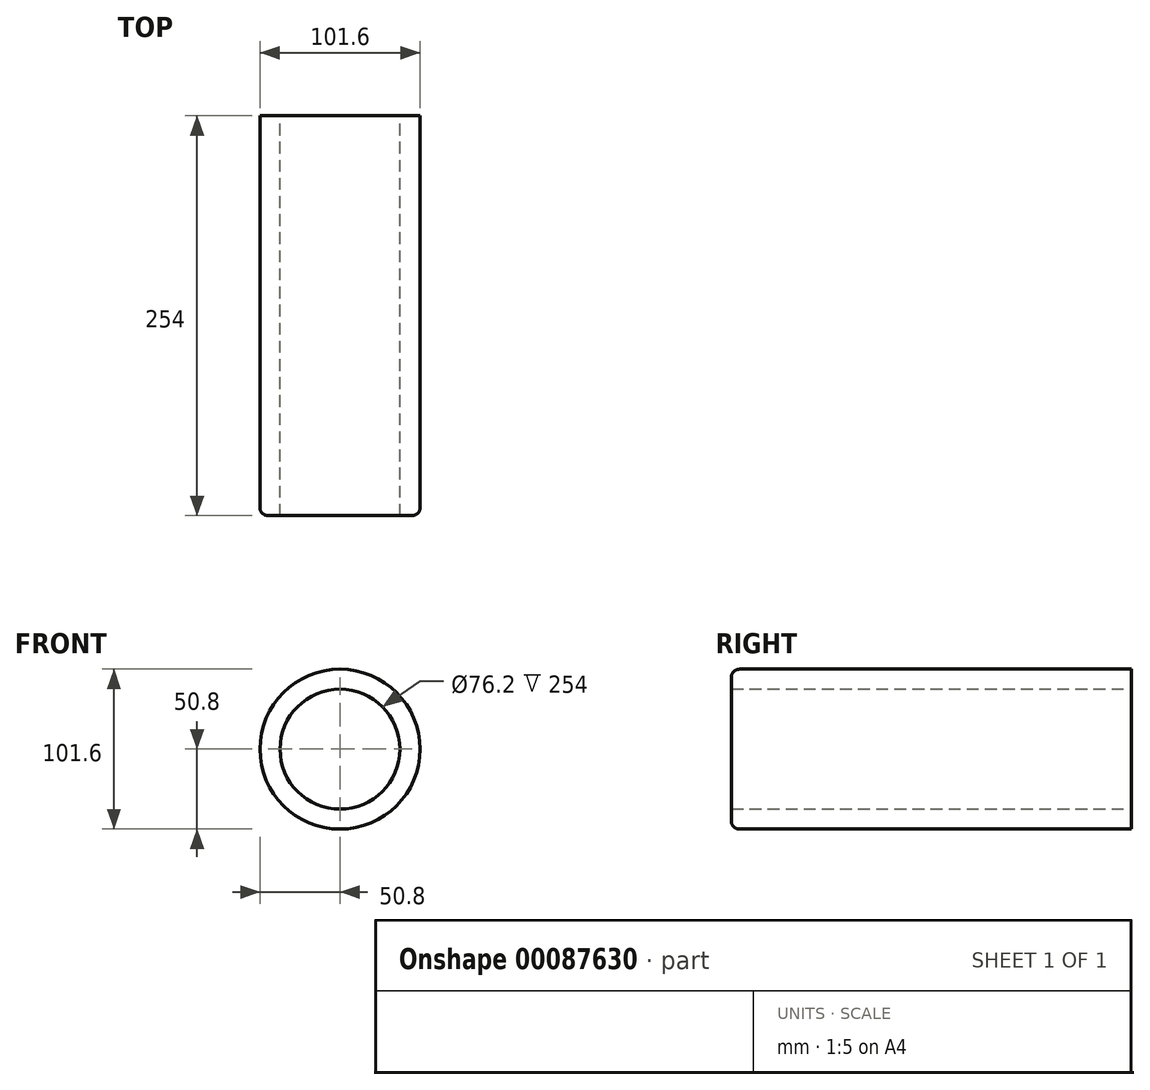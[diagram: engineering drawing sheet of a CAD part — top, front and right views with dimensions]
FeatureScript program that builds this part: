
annotation { "Feature Type Name" : "Feature", "Feature Type Description" : "" }
export const myFeature = defineFeature(function(context is Context, id is Id, definition is map)
    precondition{}
    {
        {
            var Q0;
            Q0=qCreatedBy(makeId("Front.planeOp"),FACE);
            var sketch = newSketch(context, id + "F0", { "sketchPlane" : qUnion([Q0])});
            skCircle(sketch, "E0", {"center": v(0, 0) * mm, "radius": 50.8 * mm});
            skCircle(sketch, "E1", {"center": v(0, 0) * mm, "radius": 38.1 * mm});
            skSolve(sketch);
        }
        {
            var Q0;
            Q0=makeQuery(id+"F0.imprint","IMPRINT",FACE,{"disambiguationData":[TD([[makeQuery(id+"F0.imprint","IMPRINT",EDGE,{"derivedFrom":sQuery(id+"F0.wireOp",EDGE,"E0")}),1.0]])]});
            extrude(context, id + "F1", {"entities" : qUnion([Q0]), "depth" : 254 * mm});
        }
        {
            var Q0;
            Q0=makeQuery(id+"F1.opExtrude","CAP_EDGE",EDGE,{"disambiguationData":[OSD([sQuery(id+"F0.wireOp",EDGE,"E0")])],"isStart":false});
            fillet(context, id + "F2", {"entities" : qUnion([Q0]), "radius" : 5.08 * mm, "tangentPropagation" : true, "allowEdgeOverflow" : false});
        }
    });
